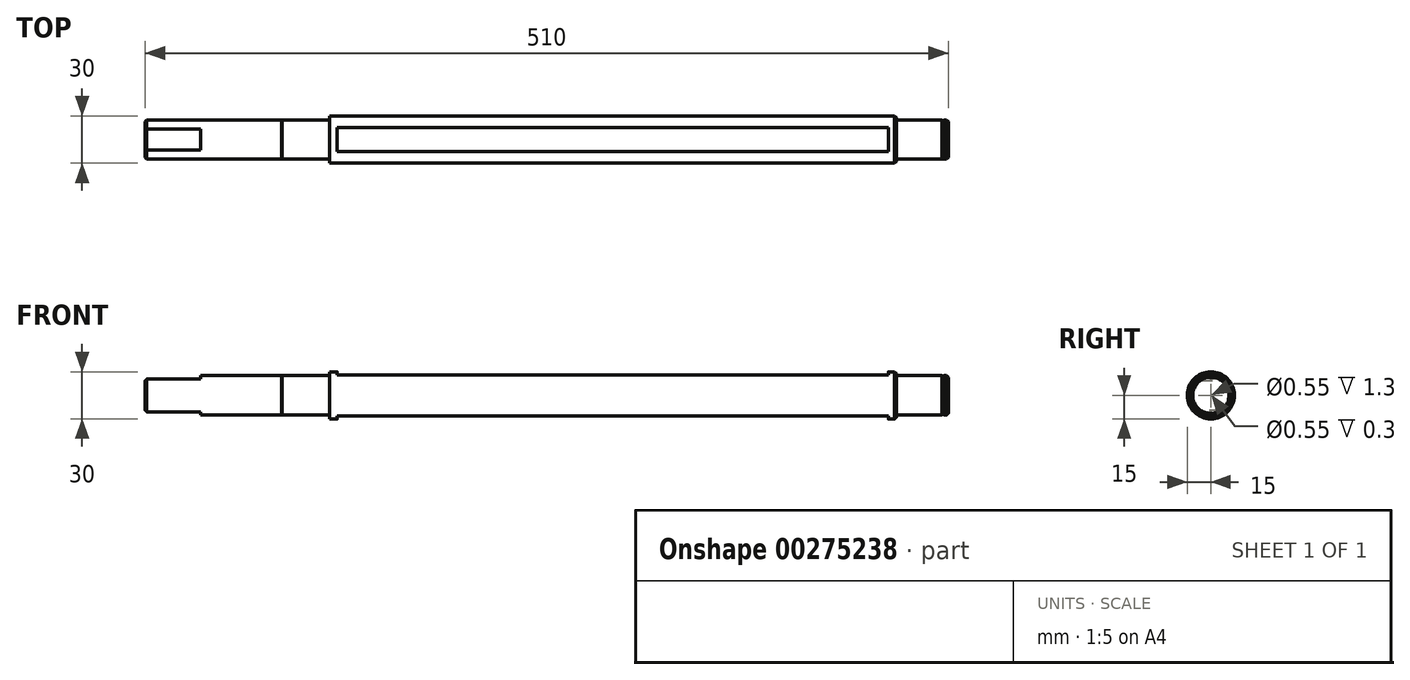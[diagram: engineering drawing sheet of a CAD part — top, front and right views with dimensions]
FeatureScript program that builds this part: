
annotation { "Feature Type Name" : "Feature", "Feature Type Description" : "" }
export const myFeature = defineFeature(function(context is Context, id is Id, definition is map)
    precondition{}
    {
        {
            var Q0;
            Q0=qCreatedBy(makeId("Front.planeOp"),FACE);
            var sketch = newSketch(context, id + "F0", { "sketchPlane" : qUnion([Q0])});
            skPoint(sketch, "E0.bottom.start.orphan", {"position": v(0, 0) * mm});
            skLineSegment(sketch, "E1", {"start": v(0, 0) * mm, "end": v(0, 15) * mm});
            skLineSegment(sketch, "E2", {"start": v(0, 15) * mm, "end": v(360, 15) * mm});
            skLineSegment(sketch, "E3", {"start": v(360, 15) * mm, "end": v(360, 0) * mm});
            skLineSegment(sketch, "E4", {"start": v(-30, 12.5) * mm, "end": v(-30, 0) * mm});
            skLineSegment(sketch, "E5", {"start": v(-30, 12.5) * mm, "end": v(0, 12.5) * mm});
            skLineSegment(sketch, "E6", {"start": v(-30, 0) * mm, "end": v(360, 0) * mm});
            skLineSegment(sketch, "E7", {"start": v(-30.3, 12.5) * mm, "end": v(-30.3, 0) * mm});
            skLineSegment(sketch, "E8", {"start": v(-30.3, 12.22) * mm, "end": v(-30, 12.22) * mm});
            skLineSegment(sketch, "E9", {"start": v(-30.3, 0.28) * mm, "end": v(-30, 0.28) * mm});
            skLineSegment(sketch, "E10", {"start": v(-48.3, 6.25) * mm, "end": v(438.56, 6.25) * mm, "construction": true});
            skPoint(sketch, "E10.startSnap0", {"position": v(-30.3, 6.25) * mm});
            skLineSegment(sketch, "E11", {"start": v(-30.3, 12.5) * mm, "end": v(-117, 12.5) * mm});
            skLineSegment(sketch, "E12", {"start": v(-30.3, 0) * mm, "end": v(-117, 0) * mm});
            skLineSegment(sketch, "E13", {"start": v(-117, 12.5) * mm, "end": v(-117, 0) * mm});
            skLineSegment(sketch, "E14", {"start": v(360, 12.5) * mm, "end": v(389, 12.5) * mm});
            skLineSegment(sketch, "E15", {"start": v(389, 12.5) * mm, "end": v(389, 0) * mm});
            skLineSegment(sketch, "E16", {"start": v(389, 0) * mm, "end": v(360, 0) * mm});
            skLineSegment(sketch, "E17", {"start": v(390.3, 12.22) * mm, "end": v(389, 12.22) * mm});
            skLineSegment(sketch, "E18", {"start": v(390.3, 0.28) * mm, "end": v(389, 0.28) * mm});
            skLineSegment(sketch, "E19", {"start": v(390.3, 12.5) * mm, "end": v(390.3, 0) * mm});
            skLineSegment(sketch, "E20", {"start": v(390.3, 12.5) * mm, "end": v(393, 12.5) * mm});
            skLineSegment(sketch, "E21", {"start": v(393, 12.5) * mm, "end": v(393, 0) * mm});
            skLineSegment(sketch, "E22", {"start": v(393, 0) * mm, "end": v(390.3, 0) * mm});
            skSolve(sketch);
        }
        {
            var Q0;
            Q0 = qSketchRegion(id + "F0", true);
            var Q1;
            Q1=sQuery(id+"F0.wireOp",EDGE,"E6");
            revolve(context, id + "F1", {"entities" : qUnion([Q0]), "axis" : qUnion([Q1]), "revolveType" : RevolveType.FULL});
        }
        {
            var Q0;
            Q0=makeQuery(id+"F1.opRevolve","SWEPT_FACE",FACE,{"disambiguationData":[OSD([sQuery(id+"F0.wireOp",EDGE,"E3")])]});
            cPlane(context, id + "F2", {"entities" : qUnion([Q0]), "cplaneType" : CPlaneType.OFFSET, "offset" : 5 * mm, "oppositeDirection" : true, "width" : 150 * mm, "height" : 150 * mm});
        }
        {
            var Q0;
            Q0=qCreatedBy(id+"F2.planeOp",FACE);
            var sketch = newSketch(context, id + "F3", { "sketchPlane" : qUnion([Q0])});
            skLineSegment(sketch, "E23", {"start": v(-7.52, 13) * mm, "end": v(7.48, 13) * mm});
            skLineSegment(sketch, "E24", {"start": v(-7.52, -13) * mm, "end": v(7.48, -13) * mm});
            skCircle(sketch, "E25.0", {"center": v(0, 0) * mm, "radius": 15 * mm});
            skSolve(sketch);
        }
        {
            var Q0;
            {var subQ0=sQuery(id+"F3.wireOp",EDGE,"E25.0");var subQ1=sQuery(id+"F3.wireOp",EDGE,"E23");var subQ2=makeQuery(id+"F3.imprint","INTERSECT",VERTEX,{"disambiguationData":[OD(0.0)],"derivedFrom":[subQ1,subQ0]});Q0=makeQuery(id+"F3.imprint","IMPRINT",FACE,{"disambiguationData":[TD([[makeQuery(id+"F3.imprint","IMPRINT",EDGE,{"disambiguationData":[TD([[subQ2,1.0]])],"derivedFrom":subQ1}),1.0]])]});}
            var Q1;
            {var subQ0=sQuery(id+"F3.wireOp",EDGE,"E25.0");var subQ1=sQuery(id+"F3.wireOp",EDGE,"E24");var subQ2=makeQuery(id+"F3.imprint","INTERSECT",VERTEX,{"disambiguationData":[OD(0.0)],"derivedFrom":[subQ1,subQ0]});Q1=makeQuery(id+"F3.imprint","IMPRINT",FACE,{"disambiguationData":[TD([[makeQuery(id+"F3.imprint","IMPRINT",EDGE,{"disambiguationData":[TD([[subQ2,1.0]])],"derivedFrom":subQ1}),-1.0]])]});}
            extrude(context, id + "F4", {"entities" : qUnion([Q0, Q1]), "operationType" : NewBodyOperationType.REMOVE, "oppositeDirection" : true, "depth" : 350 * mm});
        }
        {
            var Q0;
            Q0=makeQuery(id+"F1.opRevolve","SWEPT_FACE",FACE,{"disambiguationData":[OSD([sQuery(id+"F0.wireOp",EDGE,"E13")])]});
            var sketch = newSketch(context, id + "F5", { "sketchPlane" : qUnion([Q0])});
            skArc(sketch, "E26.0", {"start": v(-6.78, -10.5) * mm, "mid": v(0, -12.5) * mm, "end": v(6.78, -10.5) * mm});
            skLineSegment(sketch, "E27", {"start": v(-6.78, 10.5) * mm, "end": v(6.78, 10.5) * mm});
            skLineSegment(sketch, "E28", {"start": v(-6.78, -10.5) * mm, "end": v(6.78, -10.5) * mm});
            skArc(sketch, "E29.trimOffspring", {"start": v(6.78, 10.5) * mm, "mid": v(0, 12.5) * mm, "end": v(-6.78, 10.5) * mm});
            skSolve(sketch);
        }
        {
            var Q0;
            Q0=makeQuery(id+"F5.imprint","IMPRINT",FACE,{"disambiguationData":[TD([[makeQuery(id+"F5.imprint","IMPRINT",EDGE,{"derivedFrom":sQuery(id+"F5.wireOp",EDGE,"E27")}),1.0]])]});
            var Q1;
            Q1=makeQuery(id+"F5.imprint","IMPRINT",FACE,{"disambiguationData":[TD([[makeQuery(id+"F5.imprint","IMPRINT",EDGE,{"derivedFrom":sQuery(id+"F5.wireOp",EDGE,"E26.0")}),1.0]])]});
            extrude(context, id + "F6", {"entities" : qUnion([Q0, Q1]), "operationType" : NewBodyOperationType.REMOVE, "oppositeDirection" : true, "depth" : 35 * mm});
        }
        {
            var Q0;
            Q0=makeQuery(id+"F1.opRevolve","SWEPT_FACE",FACE,{"disambiguationData":[OSD([sQuery(id+"F0.wireOp",EDGE,"E13")])]});
            var Q1;
            Q1=makeQuery(id+"F1.opRevolve","SWEPT_EDGE",EDGE,{"disambiguationData":[OSD([sQuery(id+"F0.wireOp",EDGE,"E20"),sQuery(id+"F0.wireOp",EDGE,"E21")])]});
            var Q2;
            Q2=makeQuery(id+"F1.opRevolve","SWEPT_EDGE",EDGE,{"disambiguationData":[OSD([sQuery(id+"F0.wireOp",EDGE,"E2"),sQuery(id+"F0.wireOp",EDGE,"E3")])]});
            chamfer(context, id + "F7", {"entities" : qUnion([Q0, Q1, Q2]), "chamferType" : ChamferType.OFFSET_ANGLE, "width" : 1 * mm, "oppositeDirection" : false, "angle" : 45 * degree, "tangentPropagation" : true});
        }
    });
